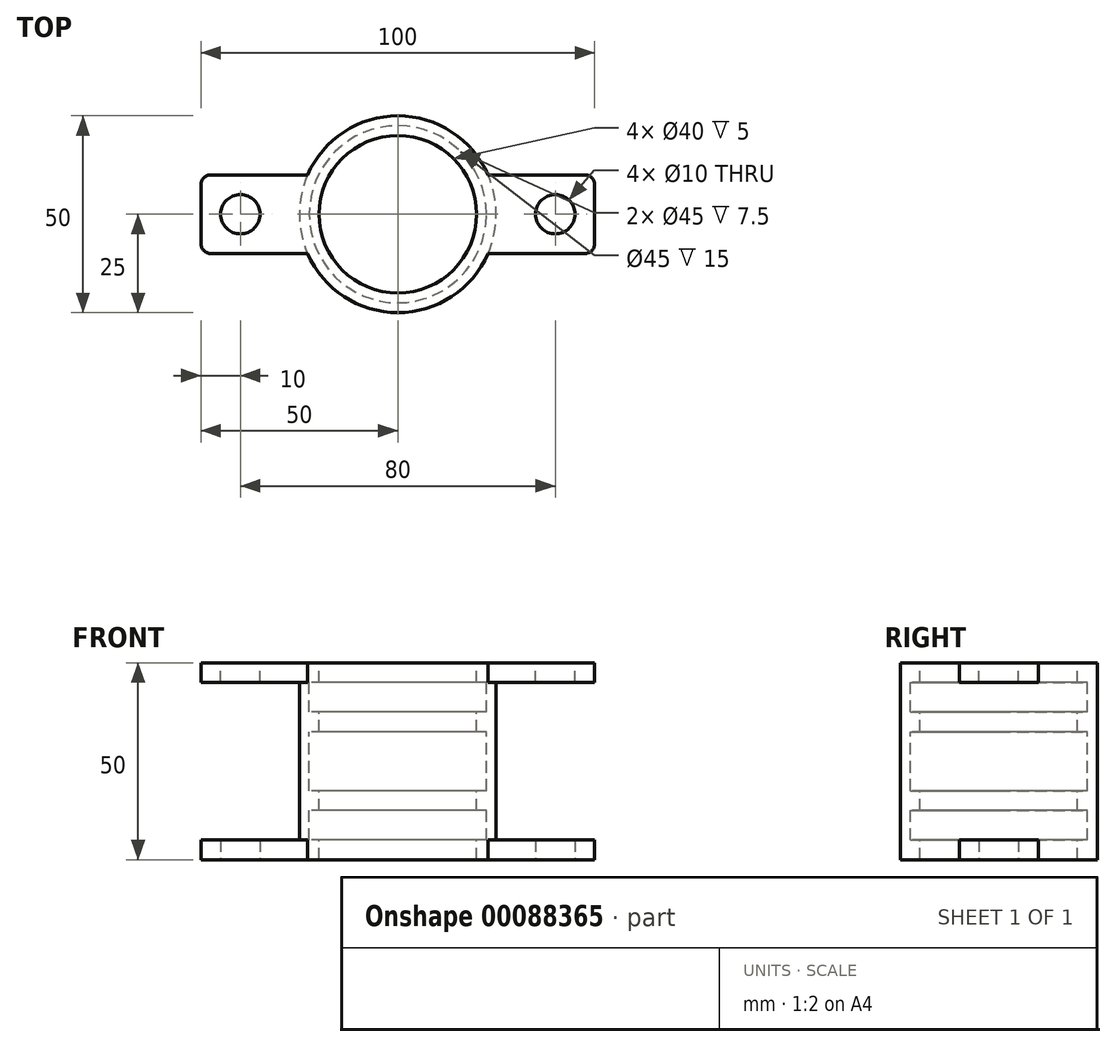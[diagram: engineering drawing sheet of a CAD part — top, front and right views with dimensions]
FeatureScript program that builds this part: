
annotation { "Feature Type Name" : "Feature", "Feature Type Description" : "" }
export const myFeature = defineFeature(function(context is Context, id is Id, definition is map)
    precondition{}
    {
        {
            var Q0;
            Q0=qCreatedBy(makeId("Front.planeOp"),FACE);
            var sketch = newSketch(context, id + "F0", { "sketchPlane" : qUnion([Q0])});
            skLineSegment(sketch, "E0", {"start": v(0, 0) * mm, "end": v(-25, 0) * mm, "construction": true});
            skLineSegment(sketch, "E1", {"start": v(-22.5, 0) * mm, "end": v(-22.5, 54.84) * mm, "construction": true});
            skLineSegment(sketch, "E2.0", {"start": v(-20, 0) * mm, "end": v(-20, 54.84) * mm, "construction": true});
            skLineSegment(sketch, "E3", {"start": v(-25, 0) * mm, "end": v(-25, 25) * mm});
            skLineSegment(sketch, "E4", {"start": v(-22.5, 0) * mm, "end": v(-22.5, 7.5) * mm});
            skLineSegment(sketch, "E5", {"start": v(-22.5, 7.5) * mm, "end": v(-20, 7.5) * mm});
            skLineSegment(sketch, "E6", {"start": v(-20, 7.5) * mm, "end": v(-20, 12.5) * mm});
            skLineSegment(sketch, "E7", {"start": v(-20, 12.5) * mm, "end": v(-22.5, 12.5) * mm});
            skLineSegment(sketch, "E8", {"start": v(-22.5, 12.5) * mm, "end": v(-22.5, 20) * mm});
            skLineSegment(sketch, "E9", {"start": v(-22.5, 20) * mm, "end": v(-20, 20) * mm});
            skLineSegment(sketch, "E10", {"start": v(-20, 20) * mm, "end": v(-20, 25) * mm});
            skLineSegment(sketch, "E11", {"start": v(-20, 25) * mm, "end": v(-25, 25) * mm});
            skLineSegment(sketch, "E12", {"start": v(-22.5, 0) * mm, "end": v(-25, 0) * mm});
            skLineSegment(sketch, "E13.MirrorCS", {"start": v(-20, -12.5) * mm, "end": v(-22.5, -12.5) * mm});
            skLineSegment(sketch, "E14.MirrorCS", {"start": v(-22.5, -12.5) * mm, "end": v(-22.5, -20) * mm});
            skLineSegment(sketch, "E15.MirrorCS", {"start": v(-25, 0) * mm, "end": v(-25, -25) * mm});
            skLineSegment(sketch, "E16.MirrorCS", {"start": v(-20, -25) * mm, "end": v(-25, -25) * mm});
            skLineSegment(sketch, "E17.MirrorCS", {"start": v(-22.5, -20) * mm, "end": v(-20, -20) * mm});
            skLineSegment(sketch, "E18.MirrorCS", {"start": v(-20, -7.5) * mm, "end": v(-20, -12.5) * mm});
            skLineSegment(sketch, "E19.MirrorCS", {"start": v(-20, -20) * mm, "end": v(-20, -25) * mm});
            skLineSegment(sketch, "E20.MirrorCS", {"start": v(-22.5, 0) * mm, "end": v(-22.5, -7.5) * mm});
            skLineSegment(sketch, "E21.MirrorCS", {"start": v(-22.5, -7.5) * mm, "end": v(-20, -7.5) * mm});
            skLineSegment(sketch, "E22", {"start": v(0, 63.98) * mm, "end": v(0, -48.98) * mm, "construction": true});
            skSolve(sketch);
        }
        {
            var Q0;
            Q0 = qSketchRegion(id + "F0", true);
            var Q1;
            Q1=sQuery(id+"F0.wireOp",EDGE,"E22");
            revolve(context, id + "F1", {"entities" : qUnion([Q0]), "axis" : qUnion([Q1]), "revolveType" : RevolveType.FULL});
        }
        {
            var Q0;
            Q0=makeQuery(id+"F1.opRevolve","SWEPT_FACE",FACE,{"disambiguationData":[OSD([sQuery(id+"F0.wireOp",EDGE,"E11")])]});
            var sketch = newSketch(context, id + "F2", { "sketchPlane" : qUnion([Q0])});
            skLineSegment(sketch, "E23", {"start": v(0, 0) * mm, "end": v(-50, 0) * mm, "construction": true});
            skArc(sketch, "E24", {"start": v(-22.91, 10) * mm, "mid": v(-25, 0) * mm, "end": v(-22.91, -10) * mm});
            skPoint(sketch, "E25", {"position": v(-25, 0) * mm});
            skLineSegment(sketch, "E26", {"start": v(-22.91, 10) * mm, "end": v(-47.5, 10) * mm});
            skLineSegment(sketch, "E27", {"start": v(-50, 0) * mm, "end": v(-50, 18.16) * mm, "construction": true});
            skLineSegment(sketch, "E28", {"start": v(-50, 7.5) * mm, "end": v(-50, 0) * mm});
            skPoint(sketch, "E29.visualSharp", {"position": v(-50, 10) * mm});
            skArc(sketch, "E29.filletArc", {"start": v(-47.5, 10) * mm, "mid": v(-49.27, 9.27) * mm, "end": v(-50, 7.5) * mm});
            skArc(sketch, "E30.MirrorCS", {"start": v(-47.5, -10) * mm, "mid": v(-49.27, -9.27) * mm, "end": v(-50, -7.5) * mm});
            skPoint(sketch, "E31.MirrorP", {"position": v(-50, -10) * mm});
            skLineSegment(sketch, "E32.MirrorCS", {"start": v(-22.91, -10) * mm, "end": v(-47.5, -10) * mm});
            skLineSegment(sketch, "E33.MirrorCS", {"start": v(-50, -7.5) * mm, "end": v(-50, 0) * mm});
            skPoint(sketch, "E34", {"position": v(-45, 0) * mm});
            skCircle(sketch, "E35", {"center": v(-40, 0) * mm, "radius": 5 * mm});
            skSolve(sketch);
        }
        {
            var Q0;
            Q0 = qSketchRegion(id + "F2", true);
            extrude(context, id + "F3", {"entities" : qUnion([Q0]), "oppositeDirection" : true, "depth" : 5 * mm});
        }
        {
            var Q0;
            Q0=makeQuery(id+"F3.opExtrude","SWEPT_BODY",BODY,{"disambiguationData":[OSD([sQuery(id+"F2.wireOp",EDGE,"E24"),sQuery(id+"F2.wireOp",EDGE,"E26"),sQuery(id+"F2.wireOp",EDGE,"E28"),sQuery(id+"F2.wireOp",EDGE,"E29.filletArc"),sQuery(id+"F2.wireOp",EDGE,"E30.MirrorCS"),sQuery(id+"F2.wireOp",EDGE,"E32.MirrorCS"),sQuery(id+"F2.wireOp",EDGE,"E33.MirrorCS"),sQuery(id+"F2.wireOp",EDGE,"E35")])]});
            var Q1;
            Q1=qCreatedBy(makeId("Right.planeOp"),FACE);
            mirror(context, id + "F4", {"entities" : qUnion([Q0]), "mirrorPlane" : qUnion([Q1])});
        }
        {
            var Q0;
            Q0=makeQuery(id+"F3.opExtrude","SWEPT_BODY",BODY,{"disambiguationData":[OSD([sQuery(id+"F2.wireOp",EDGE,"E24"),sQuery(id+"F2.wireOp",EDGE,"E26"),sQuery(id+"F2.wireOp",EDGE,"E28"),sQuery(id+"F2.wireOp",EDGE,"E29.filletArc"),sQuery(id+"F2.wireOp",EDGE,"E30.MirrorCS"),sQuery(id+"F2.wireOp",EDGE,"E32.MirrorCS"),sQuery(id+"F2.wireOp",EDGE,"E33.MirrorCS"),sQuery(id+"F2.wireOp",EDGE,"E35")])]});
            var Q1;
            Q1=makeQuery(id+"F4.opPattern","COPY",BODY,{"derivedFrom":makeQuery(id+"F3.opExtrude","SWEPT_BODY",BODY,{"disambiguationData":[OSD([sQuery(id+"F2.wireOp",EDGE,"E24"),sQuery(id+"F2.wireOp",EDGE,"E26"),sQuery(id+"F2.wireOp",EDGE,"E28"),sQuery(id+"F2.wireOp",EDGE,"E29.filletArc"),sQuery(id+"F2.wireOp",EDGE,"E30.MirrorCS"),sQuery(id+"F2.wireOp",EDGE,"E32.MirrorCS"),sQuery(id+"F2.wireOp",EDGE,"E33.MirrorCS"),sQuery(id+"F2.wireOp",EDGE,"E35")])]}),"instanceName":"1"});
            var Q2;
            Q2=qCreatedBy(makeId("Top.planeOp"),FACE);
            mirror(context, id + "F5", {"operationType" : NewBodyOperationType.ADD, "entities" : qUnion([Q0, Q1]), "mirrorPlane" : qUnion([Q2])});
        }
    });
